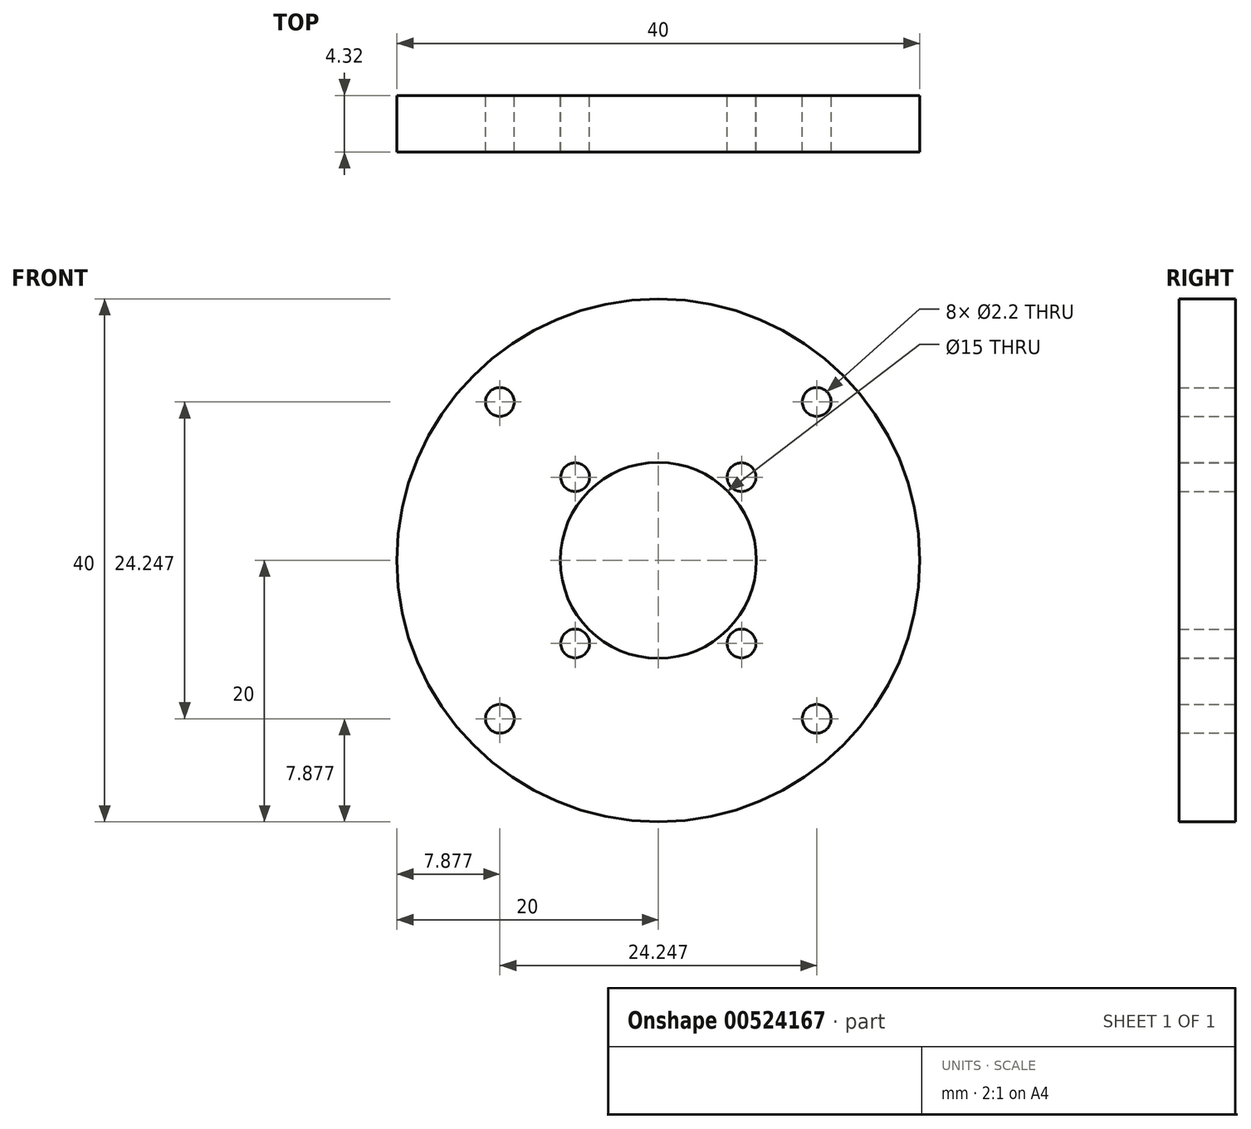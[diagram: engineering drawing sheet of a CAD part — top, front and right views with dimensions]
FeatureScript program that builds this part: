
annotation { "Feature Type Name" : "Feature", "Feature Type Description" : "" }
export const myFeature = defineFeature(function(context is Context, id is Id, definition is map)
    precondition{}
    {
        {
            var Q0;
            Q0=qCreatedBy(makeId("Front.planeOp"),FACE);
            var sketch = newSketch(context, id + "F0", { "sketchPlane" : qUnion([Q0])});
            skCircle(sketch, "E0", {"center": v(0, 0) * mm, "radius": 20 * mm});
            skCircle(sketch, "E1", {"center": v(0, 0) * mm, "radius": 7.5 * mm});
            skCircle(sketch, "E2", {"center": v(0, 0) * mm, "radius": 9 * mm, "construction": true});
            skLineSegment(sketch, "E3", {"start": v(0, 0) * mm, "end": v(6.36, 6.36) * mm, "construction": true});
            skCircle(sketch, "E4", {"center": v(6.36, 6.36) * mm, "radius": 1.1 * mm});
            skCircle(sketch, "E5.1.0", {"center": v(-6.36, 6.36) * mm, "radius": 1.1 * mm});
            skCircle(sketch, "E5.2.0", {"center": v(-6.36, -6.36) * mm, "radius": 1.1 * mm});
            skCircle(sketch, "E5.3.0", {"center": v(6.36, -6.36) * mm, "radius": 1.1 * mm});
            skCircle(sketch, "E6", {"center": v(0, 0) * mm, "radius": 17.15 * mm, "construction": true});
            skLineSegment(sketch, "E7", {"start": v(0, 0) * mm, "end": v(12.12, 12.12) * mm, "construction": true});
            skCircle(sketch, "E8", {"center": v(12.12, 12.12) * mm, "radius": 1.1 * mm});
            skCircle(sketch, "E9.1.0", {"center": v(-12.12, 12.12) * mm, "radius": 1.1 * mm});
            skCircle(sketch, "E9.2.0", {"center": v(-12.12, -12.12) * mm, "radius": 1.1 * mm});
            skCircle(sketch, "E9.3.0", {"center": v(12.12, -12.12) * mm, "radius": 1.1 * mm});
            skSolve(sketch);
        }
        {
            var Q0;
            Q0=qSketchRegion(id+"F0",true);
            extrude(context, id + "F1", {"entities" : qUnion([Q0]), "depth" : 4.32 * mm});
        }
    });
